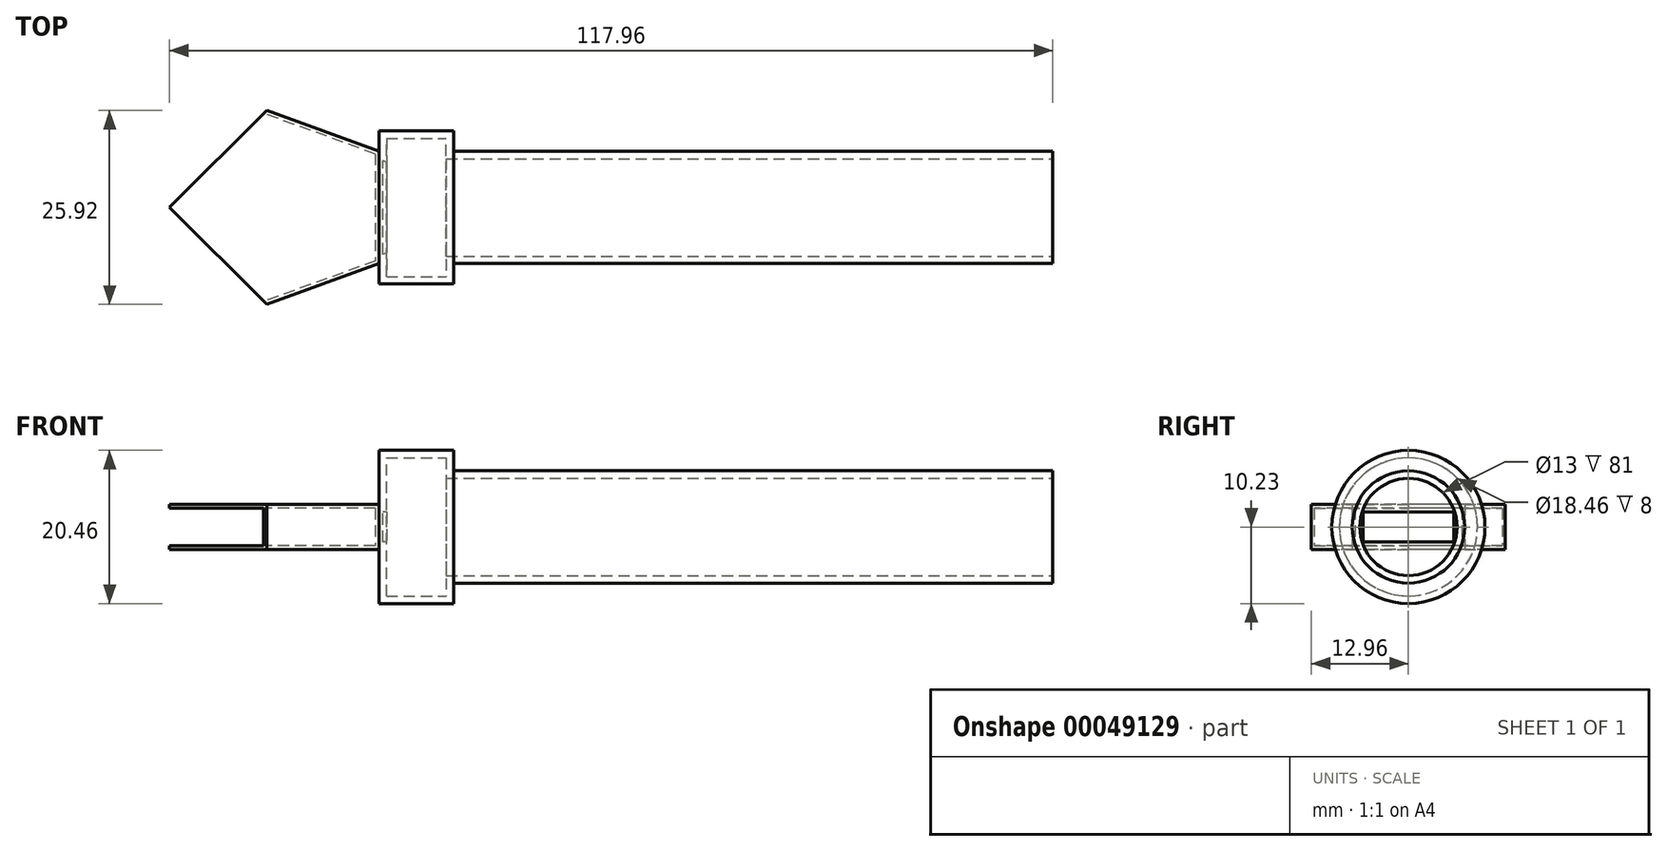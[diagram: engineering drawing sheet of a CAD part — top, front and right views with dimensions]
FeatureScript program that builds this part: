
annotation { "Feature Type Name" : "Feature", "Feature Type Description" : "" }
export const myFeature = defineFeature(function(context is Context, id is Id, definition is map)
    precondition{}
    {
        {
            var Q0;
            Q0=qCreatedBy(makeId("Top.planeOp"),FACE);
            var sketch = newSketch(context, id + "F0", { "sketchPlane" : qUnion([Q0])});
            skLineSegment(sketch, "E0", {"start": v(-19.66, 7.5) * mm, "end": v(-19.66, 0) * mm});
            skLineSegment(sketch, "E1", {"start": v(-19.66, 7.5) * mm, "end": v(-34.66, 12.96) * mm});
            skLineSegment(sketch, "E2", {"start": v(-34.66, 12.96) * mm, "end": v(-47.62, 0) * mm});
            skLineSegment(sketch, "E3", {"start": v(-9.66, 7.5) * mm, "end": v(70.34, 7.5) * mm});
            skLineSegment(sketch, "E4", {"start": v(70.34, 7.5) * mm, "end": v(70.34, 0) * mm});
            skLineSegment(sketch, "E5", {"start": v(70.34, 0) * mm, "end": v(-47.62, 0) * mm});
            skLineSegment(sketch, "E6.MirrorCS", {"start": v(-34.66, -12.96) * mm, "end": v(-47.62, 0) * mm});
            skLineSegment(sketch, "E7.MirrorCS", {"start": v(-19.66, -7.5) * mm, "end": v(-19.66, 0) * mm});
            skLineSegment(sketch, "E8.MirrorCS", {"start": v(-19.66, -7.5) * mm, "end": v(-34.66, -12.96) * mm});
            skLineSegment(sketch, "E9", {"start": v(-19.66, 7.5) * mm, "end": v(-19.66, 10.23) * mm});
            skPoint(sketch, "E9.endSnap0", {"position": v(-27.16, 10.23) * mm});
            skLineSegment(sketch, "E10", {"start": v(-19.66, 10.23) * mm, "end": v(-9.66, 10.23) * mm});
            skLineSegment(sketch, "E11", {"start": v(-9.66, 10.23) * mm, "end": v(-9.66, 0) * mm});
            skSolve(sketch);
        }
        {
            var Q0;
            {var subQ2=sQuery(id+"F0.wireOp",EDGE,"E0");Q0=makeQuery(id+"F0.imprint","IMPRINT",FACE,{"disambiguationData":[TD([[makeQuery(id+"F0.imprint","IMPRINT",EDGE,{"derivedFrom":subQ2}),-1.0]])]});}
            var Q1;
            {var subQ1=sQuery(id+"F0.wireOp",EDGE,"E6.MirrorCS");Q1=makeQuery(id+"F0.imprint","IMPRINT",FACE,{"disambiguationData":[TD([[makeQuery(id+"F0.imprint","IMPRINT",EDGE,{"derivedFrom":subQ1}),-1.0]])]});}
            extrude(context, id + "F1", {"entities" : qUnion([Q0, Q1]), "depth" : 3 * mm, "hasSecondDirection" : true, "secondDirectionOppositeDirection" : true, "secondDirectionDepth" : 3 * mm});
        }
        {
            var Q0;
            Q0=makeQuery(id+"F1.opExtrude","SWEPT_FACE",FACE,{"disambiguationData":[OSD([sQuery(id+"F0.wireOp",EDGE,"E2")])]});
            var Q1;
            Q1=makeQuery(id+"F1.opExtrude","SWEPT_FACE",FACE,{"disambiguationData":[OSD([sQuery(id+"F0.wireOp",EDGE,"E5")])]});
            var Q2;
            Q2=makeQuery(id+"F1.opExtrude","SWEPT_FACE",FACE,{"disambiguationData":[OSD([sQuery(id+"F0.wireOp",EDGE,"E6.MirrorCS")])]});
            shell(context, id + "F2", {"entities" : qUnion([Q0, Q1, Q2]), "thickness" : 0.5 * mm});
        }
        {
            var Q0;
            {var subQ4=sQuery(id+"F0.wireOp",EDGE,"E0");Q0=makeQuery(id+"F0.imprint","IMPRINT",FACE,{"disambiguationData":[TD([[makeQuery(id+"F0.imprint","IMPRINT",EDGE,{"derivedFrom":subQ4}),1.0]])]});}
            var Q1;
            {var subQ4=sQuery(id+"F0.wireOp",EDGE,"E3");Q1=makeQuery(id+"F0.imprint","IMPRINT",FACE,{"disambiguationData":[TD([[makeQuery(id+"F0.imprint","IMPRINT",EDGE,{"derivedFrom":subQ4}),-1.0]])]});}
            var Q2;
            Q2=sQuery(id+"F0.wireOp",EDGE,"E5");
            revolve(context, id + "F3", {"operationType" : NewBodyOperationType.ADD, "entities" : qUnion([Q0, Q1]), "axis" : qUnion([Q2]), "revolveType" : RevolveType.FULL});
        }
        {
            var Q0;
            Q0=makeQuery(id+"F3.opRevolve","SWEPT_FACE",FACE,{"disambiguationData":[OSD([sQuery(id+"F0.wireOp",EDGE,"E4")])]});
            shell(context, id + "F4", {"entities" : qUnion([Q0]), "thickness" : 1 * mm});
        }
    });
